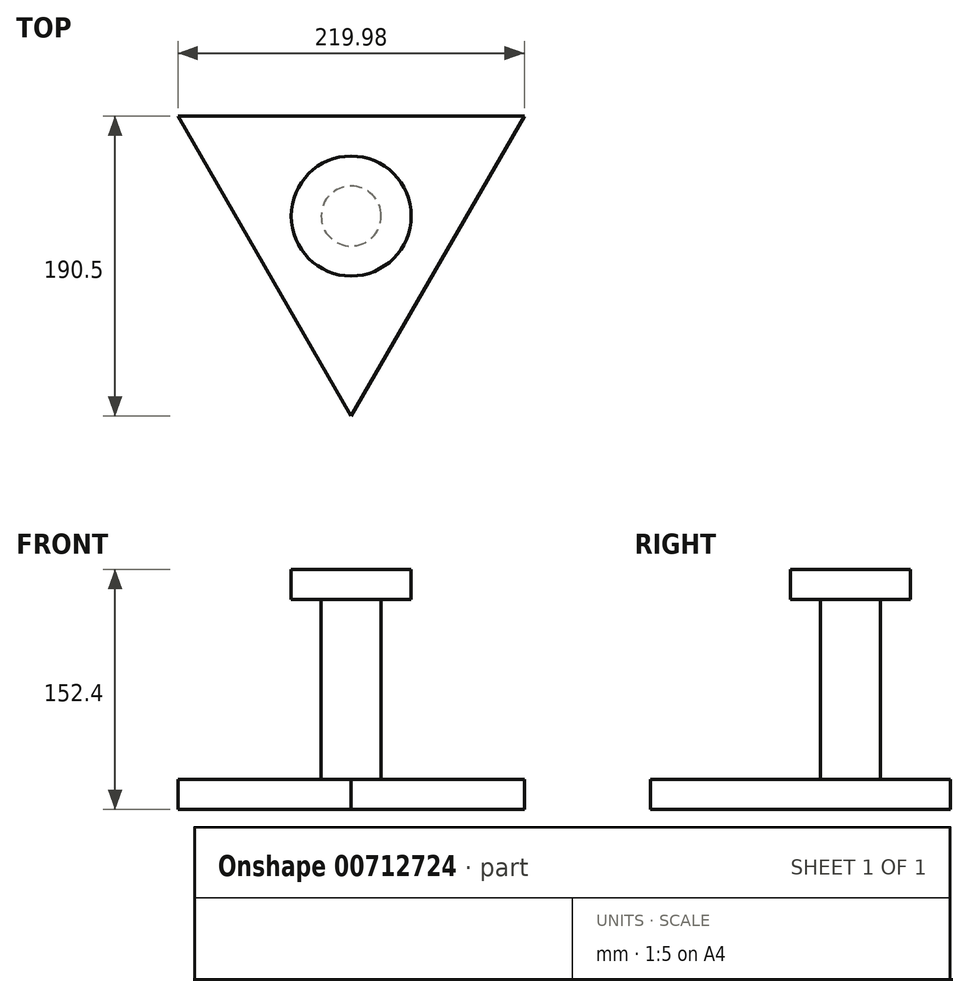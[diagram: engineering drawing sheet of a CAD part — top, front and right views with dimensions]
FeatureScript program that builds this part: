
annotation { "Feature Type Name" : "Feature", "Feature Type Description" : "" }
export const myFeature = defineFeature(function(context is Context, id is Id, definition is map)
    precondition{}
    {
        {
            var Q0;
            Q0=qCreatedBy(makeId("Top.planeOp"),FACE);
            var sketch = newSketch(context, id + "F0", { "sketchPlane" : qUnion([Q0])});
            skCircle(sketch, "E0.cCircle", {"center": v(0, 0) * mm, "radius": 127 * mm, "construction": true});
            skLineSegment(sketch, "E0.0", {"start": v(0, -127) * mm, "end": v(-109.99, 63.5) * mm});
            skLineSegment(sketch, "E0.1", {"start": v(-109.99, 63.5) * mm, "end": v(109.99, 63.5) * mm});
            skLineSegment(sketch, "E0.2", {"start": v(109.99, 63.5) * mm, "end": v(0, -127) * mm});
            skSolve(sketch);
        }
        {
            var Q0;
            Q0=makeQuery(id+"F0.imprint","IMPRINT",FACE,{"disambiguationData":[TD([[makeQuery(id+"F0.imprint","IMPRINT",EDGE,{"derivedFrom":sQuery(id+"F0.wireOp",EDGE,"E0.0")}),-1.0]])]});
            extrude(context, id + "F1", {"entities" : qUnion([Q0]), "depth" : 19.05 * mm, "offsetDistance" : 25.4 * mm});
        }
        {
            var Q0;
            Q0=makeQuery(id+"F1.opExtrude","CAP_FACE",FACE,{"disambiguationData":[OSD([sQuery(id+"F0.wireOp",EDGE,"E0.0"),sQuery(id+"F0.wireOp",EDGE,"E0.1"),sQuery(id+"F0.wireOp",EDGE,"E0.2")])],"isStart":false});
            var sketch = newSketch(context, id + "F2", { "sketchPlane" : qUnion([Q0])});
            skCircle(sketch, "E1", {"center": v(0, 0) * mm, "radius": 19.05 * mm});
            skSolve(sketch);
        }
        {
            var Q0;
            Q0=makeQuery(id+"F2.imprint","IMPRINT",FACE,{"disambiguationData":[TD([[makeQuery(id+"F2.imprint","IMPRINT",EDGE,{"derivedFrom":sQuery(id+"F2.wireOp",EDGE,"E1")}),1.0]])]});
            extrude(context, id + "F3", {"entities" : qUnion([Q0]), "operationType" : NewBodyOperationType.ADD, "depth" : 114.3 * mm, "offsetDistance" : 25.4 * mm});
        }
        {
            var Q0;
            Q0=makeQuery(id+"F3.opExtrude","CAP_FACE",FACE,{"disambiguationData":[OSD([sQuery(id+"F2.wireOp",EDGE,"E1")])],"isStart":false});
            var sketch = newSketch(context, id + "F4", { "sketchPlane" : qUnion([Q0])});
            skCircle(sketch, "E2", {"center": v(0, 0) * mm, "radius": 38.1 * mm});
            skSolve(sketch);
        }
        {
            var Q0;
            Q0=makeQuery(id+"F4.imprint","IMPRINT",FACE,{"disambiguationData":[TD([[makeQuery(id+"F4.imprint","IMPRINT",EDGE,{"derivedFrom":sQuery(id+"F4.wireOp",EDGE,"E2")}),1.0]])]});
            var Q1;
            Q1=makeQuery(id+"F4.imprint","IMPRINT",FACE,{"disambiguationData":[TD([[makeQuery(id+"F4.imprint","IMPRINT",EDGE,{"derivedFrom":makeQuery(id+"F3.opExtrude","CAP_EDGE",EDGE,{"disambiguationData":[OSD([sQuery(id+"F2.wireOp",EDGE,"E1")])],"isStart":false})}),1.0]])]});
            extrude(context, id + "F5", {"entities" : qUnion([Q0, Q1]), "operationType" : NewBodyOperationType.ADD, "depth" : 19.05 * mm, "offsetDistance" : 25.4 * mm});
        }
    });
